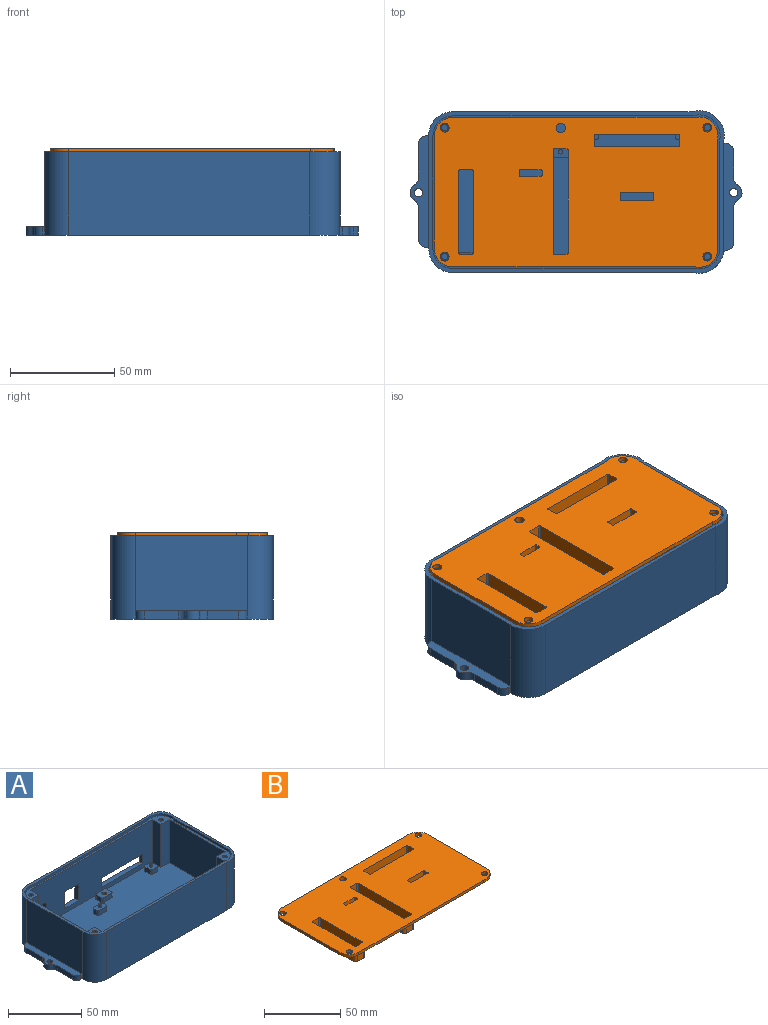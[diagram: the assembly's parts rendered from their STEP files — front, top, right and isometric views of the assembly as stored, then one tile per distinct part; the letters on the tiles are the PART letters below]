
ASSEMBLY  parts=2 mates=1
PART A: 161 faces, bbox 159x77.8x40 mm
  f0: plane 5x4mm, normal (-1,0,0), area 20mm2, adj f1,f7,f8,f9
  f1: cylinder r=1mm len=4mm, axis (0,0,-1), area 6.3mm2, adj f0,f2,f8,f9
  f2: plane 7x4mm, normal (0,-1,0), area 28mm2, adj f1,f3,f8,f9
  f3: cylinder r=1mm len=4mm, axis (0,0,-1), area 6.3mm2, adj f2,f4,f8,f9
  f4: plane 5x4mm, normal (1,0,0), area 20mm2, adj f3,f5,f8,f9
  f5: cylinder r=1mm len=4mm, axis (0,0,-1), area 6.3mm2, adj f4,f6,f8,f9
  f6: plane 7x4mm, normal (0,1,0), area 28mm2, adj f5,f7,f8,f9
  f7: cylinder r=1mm len=4mm, axis (0,0,-1), area 6.3mm2, adj f0,f6,f8,f9
  f8: plane 9x7mm, normal (0,0,1), area 54.1mm2, adj f0,f1,f2,f3,f4,f5,f6,f7
  f9: plane 134x70mm, normal (0,0,1), area 8671mm2, adj f0,f1,f2,f3,f4,f5,f6,f7
  f10: plane 4x3mm, normal (-1,0,0), area 12mm2, adj f9,f11,f17,f18
  f11: cylinder r=1mm len=4mm, axis (0,0,-1), area 6.3mm2, adj f9,f10,f12,f18
  f12: plane 7x4mm, normal (0,-1,0), area 28mm2, adj f9,f11,f13,f18
  f13: cylinder r=1mm len=4mm, axis (0,0,-1), area 6.3mm2, adj f9,f12,f14,f18
  f14: plane 4x3mm, normal (1,0,0), area 12mm2, adj f9,f13,f15,f18
  f15: cylinder r=1mm len=4mm, axis (0,0,-1), area 6.3mm2, adj f9,f14,f16,f18
  f16: plane 7x4mm, normal (0,1,0), area 28mm2, adj f9,f15,f17,f18
  f17: cylinder r=1mm len=4mm, axis (0,0,-1), area 6.3mm2, adj f9,f10,f16,f18
  f18: plane 9x5mm, normal (0,0,1), area 41mm2, adj f10,f11,f12,f13,f14,f15,f16,f17
  f19: plane 118.02x36mm, normal (0,1,0), area 4188.6mm2, adj f9,f27,f28,f32,f81,f86,f87,f89
  f20: plane 118x36mm, normal (0,-1,0), area 3578.4mm2, adj f9,f22,f23,f32,f51,f52,f53,f54
  f21: plane 114.55x40mm, normal (0,1,0), area 3912.4mm2, adj f39,f40,f49,f50,f51,f52,f53,f54
  f22: plane 36x8mm, normal (1,0,0), area 288mm2, adj f9,f20,f31,f32
  f23: plane 36x8mm, normal (-1,0,0), area 288mm2, adj f9,f20,f24,f32
  f24: plane 36x8mm, normal (0,-1,0), area 288mm2, adj f9,f23,f25,f32
  f25: plane 54x36mm, normal (-1,0,0), area 1944mm2, adj f9,f24,f26,f32
  f26: plane 36x8mm, normal (0,1,0), area 288mm2, adj f9,f25,f27,f32
  f27: plane 36x8mm, normal (-1,0,0), area 288mm2, adj f9,f19,f26,f32
  f28: plane 36x8mm, normal (1,0,0), area 288mm2, adj f9,f19,f29,f32
  f29: plane 36x7.98mm, normal (0,1,0), area 287.4mm2, adj f9,f28,f30,f32
  f30: plane 54x36mm, normal (1,0,0), area 1944mm2, adj f9,f29,f31,f32
  f31: plane 36x8mm, normal (0,-1,0), area 288mm2, adj f9,f22,f30,f32
  f32: plane 137.52x73.78mm, normal (0,0,1), area 781.4mm2, adj f19,f20,f22,f23,f24,f25,f26,f27
  f33: plane 53.16x2mm, normal (-1,0,0), area 106.3mm2, adj f32,f37,f38,f49
  f34: plane 114.86x2mm, normal (0,-1,0), area 229.7mm2, adj f32,f38,f46,f49
  f35: plane 53.44x2mm, normal (1,0,0), area 106.9mm2, adj f32,f46,f47,f49
  f36: plane 115.72x2mm, normal (0,1,0), area 231.4mm2, adj f32,f37,f47,f49
  f37: cylinder r=9.77mm len=11.8mm, axis (0,0,-1), area 30.7mm2, adj f32,f33,f36,f49
  f38: cylinder r=10.01mm len=13.15mm, axis (0,0,-1), area 44.2mm2, adj f32,f33,f34,f49
  f39: cylinder r=11.5mm len=40mm, axis (0,0,-1), area 722.6mm2, adj f21,f48,f49,f50,f127
  f40: cylinder r=12.01mm len=40mm, axis (0,0,-1), area 1034.3mm2, adj f21,f41,f49,f50,f140
  f41: plane 51.85x36mm, normal (1,0,0), area 1866.6mm2, adj f40,f42,f49,f144
  f42: extruded ~40x0.3mm, area 13.9mm2, adj f41,f43,f49,f50,f141
  f43: cylinder r=11.77mm len=40mm, axis (0,0,-1), area 777.6mm2, adj f42,f44,f49,f50
  f44: plane 115.49x40mm, normal (0,-1,0), area 4619.6mm2, adj f43,f45,f49,f50
  f45: cylinder r=11.5mm len=40mm, axis (0,0,-1), area 747.2mm2, adj f44,f48,f49,f50,f126
  f46: cylinder r=9.5mm len=9.5mm, axis (0,0,-1), area 29.8mm2, adj f32,f34,f35,f49
  f47: cylinder r=9.5mm len=10.06mm, axis (0,0,-1), area 31mm2, adj f32,f35,f36,f49
  f48: plane 53.38x36mm, normal (-1,0,0), area 1921.9mm2, adj f39,f45,f49,f133
  f49: plane 141.52x77.78mm, normal (0,0,1), area 822.7mm2, adj f21,f33,f34,f35,f36,f37,f38,f39
  f50: plane 159x77.78mm, normal (0,0,-1), area 11301.4mm2, adj f21,f39,f40,f42,f43,f44,f45,f123
  f51: plane 7.85x3.5mm, normal (1,0,0), area 27.5mm2, adj f20,f21,f52,f54
  f52: plane 40x3.5mm, normal (0,0,1), area 140mm2, adj f20,f21,f51,f53
  f53: plane 7.85x3.5mm, normal (-1,0,0), area 27.5mm2, adj f20,f21,f52,f54
  f54: plane 40x3.5mm, normal (0,0,-1), area 140mm2, adj f20,f21,f51,f53
  f55: plane 14x3.5mm, normal (1,0,0), area 49mm2, adj f20,f21,f56,f58
  f56: plane 13.4x3.5mm, normal (0,0,1), area 46.9mm2, adj f20,f21,f55,f57
  f57: plane 14x3.5mm, normal (-1,0,0), area 49mm2, adj f20,f21,f56,f58
  f58: plane 13.4x3.5mm, normal (0,0,-1), area 46.9mm2, adj f20,f21,f55,f57
  f59: plane 12x3.5mm, normal (0,0,-1), area 42mm2, adj f20,f21,f60,f62
  f60: plane 14x3.5mm, normal (1,0,0), area 49mm2, adj f20,f21,f59,f61
  f61: plane 12x3.5mm, normal (0,0,1), area 42mm2, adj f20,f21,f60,f62
  f62: plane 14x3.5mm, normal (-1,0,0), area 49mm2, adj f20,f21,f59,f61
  f63: plane 7x7mm, normal (0,0,1), area 45mm2, adj f64,f65,f66,f67,f68,f69,f70,f71
  f64: cylinder r=1mm len=4mm, axis (0,0,-1), area 6.3mm2, adj f9,f63,f65,f71
  f65: plane 5x4mm, normal (0,1,0), area 20mm2, adj f9,f63,f64,f66
  f66: cylinder r=1mm len=4mm, axis (0,0,-1), area 6.3mm2, adj f9,f63,f65,f67
  f67: plane 5x4mm, normal (1,0,0), area 20mm2, adj f9,f63,f66,f68
  f68: cylinder r=1mm len=4mm, axis (0,0,-1), area 6.3mm2, adj f9,f63,f67,f69
  f69: plane 5x4mm, normal (0,-1,0), area 20mm2, adj f9,f63,f68,f70
  f70: cylinder r=1mm len=4mm, axis (0,0,-1), area 6.3mm2, adj f9,f63,f69,f71
  f71: plane 5x4mm, normal (-1,0,0), area 20mm2, adj f9,f63,f64,f70
  f72: plane 10x7mm, normal (0,0,1), area 61.1mm2, adj f73,f74,f75,f76,f77,f78,f79,f80
  f73: cylinder r=1mm len=4mm, axis (0,0,-1), area 6.3mm2, adj f9,f72,f74,f80
  f74: plane 8x4mm, normal (0,1,0), area 32mm2, adj f9,f72,f73,f75
  f75: cylinder r=1mm len=4mm, axis (0,0,-1), area 6.3mm2, adj f9,f72,f74,f76
  f76: plane 5x4mm, normal (1,0,0), area 20mm2, adj f9,f72,f75,f77
  f77: cylinder r=1mm len=4mm, axis (0,0,-1), area 6.3mm2, adj f9,f72,f76,f78
  f78: plane 8x4mm, normal (0,-1,0), area 32mm2, adj f9,f72,f77,f79
  f79: cylinder r=1mm len=4mm, axis (0,0,-1), area 6.3mm2, adj f9,f72,f78,f80
  f80: plane 5x4mm, normal (-1,0,0), area 20mm2, adj f9,f72,f73,f79
  f81: plane 10x6mm, normal (0,0,1), area 56mm2, adj f19,f82,f83,f84,f85,f86,f87,f88
  f82: cylinder r=1mm len=4mm, axis (0,0,-1), area 6.3mm2, adj f9,f81,f83,f88
  f83: plane 8x4mm, normal (0,1,0), area 32mm2, adj f9,f81,f82,f84
  f84: cylinder r=1mm len=4mm, axis (0,0,-1), area 6.3mm2, adj f9,f81,f83,f85
  f85: plane 4x4mm, normal (1,0,0), area 16mm2, adj f9,f81,f84,f86
  f86: cylinder r=1mm len=4mm, axis (0,0,-1), area 6.3mm2, adj f9,f19,f81,f85
  f87: cylinder r=1mm len=4mm, axis (0,0,-1), area 6.3mm2, adj f9,f19,f81,f88
  f88: plane 4x4mm, normal (-1,0,0), area 16mm2, adj f9,f81,f82,f87
  f89: plane 9x6mm, normal (0,0,1), area 45.1mm2, adj f19,f90,f91,f92,f93,f94,f95,f96
  f90: cylinder r=1mm len=4mm, axis (0,0,-1), area 6.3mm2, adj f9,f19,f89,f96
  f91: cylinder r=1mm len=4mm, axis (0,0,-1), area 6.3mm2, adj f9,f19,f89,f92
  f92: plane 4x4mm, normal (-1,0,0), area 16mm2, adj f9,f89,f91,f93
  f93: cylinder r=1mm len=4mm, axis (0,0,-1), area 6.3mm2, adj f9,f89,f92,f94
  f94: plane 7x4mm, normal (0,1,0), area 28mm2, adj f9,f89,f93,f95
  f95: cylinder r=1mm len=4mm, axis (0,0,-1), area 6.3mm2, adj f9,f89,f94,f96
  f96: plane 4x4mm, normal (1,0,0), area 16mm2, adj f9,f89,f90,f95
  f97: plane 7x7mm, normal (0,0,1), area 45mm2, adj f98,f99,f100,f101,f102,f103,f104,f105
  f98: cylinder r=1mm len=4mm, axis (0,0,-1), area 6.3mm2, adj f9,f97,f99,f105
  f99: plane 5x4mm, normal (0,1,0), area 20mm2, adj f9,f97,f98,f100
  f100: cylinder r=1mm len=4mm, axis (0,0,-1), area 6.3mm2, adj f9,f97,f99,f101
  f101: plane 5x4mm, normal (1,0,0), area 20mm2, adj f9,f97,f100,f102
  f102: cylinder r=1mm len=4mm, axis (0,0,-1), area 6.3mm2, adj f9,f97,f101,f103
  f103: plane 5x4mm, normal (0,-1,0), area 20mm2, adj f9,f97,f102,f104
  f104: cylinder r=1mm len=4mm, axis (0,0,-1), area 6.3mm2, adj f9,f97,f103,f105
  f105: plane 5x4mm, normal (-1,0,0), area 20mm2, adj f9,f97,f98,f104
  f106: plane 10x7mm, normal (0,0,1), area 61.1mm2, adj f107,f108,f109,f110,f111,f112,f113,f114
  f107: cylinder r=1mm len=4mm, axis (0,0,-1), area 6.3mm2, adj f9,f106,f108,f114
  f108: plane 8x4mm, normal (0,1,0), area 32mm2, adj f9,f106,f107,f109
  f109: cylinder r=1mm len=4mm, axis (0,0,-1), area 6.3mm2, adj f9,f106,f108,f110
  f110: plane 5x4mm, normal (1,0,0), area 20mm2, adj f9,f106,f109,f111
  f111: cylinder r=1mm len=4mm, axis (0,0,-1), area 6.3mm2, adj f9,f106,f110,f112
  f112: plane 8x4mm, normal (0,-1,0), area 32mm2, adj f9,f106,f111,f113
  f113: cylinder r=1mm len=4mm, axis (0,0,-1), area 6.3mm2, adj f9,f106,f112,f114
  f114: plane 5x4mm, normal (-1,0,0), area 20mm2, adj f9,f106,f107,f113
  f115: cylinder r=1.6mm len=13mm, axis (0,0,1), area 130.7mm2, adj f32,f116
  f116: plane 3.2x3.2mm, normal (0,0,1), area 8mm2, adj f115
  f117: cylinder r=1.6mm len=13mm, axis (0,0,1), area 130.7mm2, adj f32,f118
  f118: plane 3.2x3.2mm, normal (0,0,1), area 8mm2, adj f117
  f119: cylinder r=1.6mm len=13mm, axis (0,0,1), area 130.7mm2, adj f32,f120
  f120: plane 3.2x3.2mm, normal (0,0,1), area 8mm2, adj f119
  f121: cylinder r=1.6mm len=13mm, axis (0,0,1), area 130.7mm2, adj f32,f122
  f122: plane 3.2x3.2mm, normal (0,0,1), area 8mm2, adj f121
  f123: cylinder r=4mm len=4mm, axis (0,0,-1), area 16.8mm2, adj f50,f124,f132,f133
  f124: plane 15.25x4mm, normal (-1,0,0), area 61mm2, adj f50,f123,f125,f133
  f125: cylinder r=4mm len=4mm, axis (0,0,-1), area 24.7mm2, adj f50,f124,f126,f133
  f126: plane 4x1.1mm, normal (-0.02,-1,0), area 4.4mm2, adj f45,f50,f125,f133
  f127: plane 4x1mm, normal (0,1,0), area 4mm2, adj f39,f50,f128,f133
  f128: cylinder r=4mm len=4mm, axis (0,0,-1), area 25.1mm2, adj f50,f127,f129,f133
  f129: plane 16.25x4mm, normal (-1,0,0), area 65mm2, adj f50,f128,f130,f133
  f130: cylinder r=4mm len=4mm, axis (0,0,-1), area 16.8mm2, adj f50,f129,f132,f133
  f131: cylinder r=2mm len=4mm, axis (0,0,-1), area 50.3mm2, adj f50,f133
  f132: cylinder r=4mm len=6.93mm, axis (0,0,-1), area 33.5mm2, adj f50,f123,f130,f133
  f133: plane 53.38x9mm, normal (0,0,1), area 275.1mm2, adj f48,f123,f124,f125,f126,f127,f128,f129
  f134: plane 16.91x4mm, normal (1,0,0), area 67.7mm2, adj f50,f135,f142,f144
  f135: cylinder r=4mm len=4mm, axis (0,0,-1), area 16.8mm2, adj f50,f134,f136,f144
  f136: cylinder r=4mm len=6.93mm, axis (0,0,-1), area 33.5mm2, adj f50,f135,f137,f144
  f137: cylinder r=4mm len=4mm, axis (0,0,-1), area 16.8mm2, adj f50,f136,f138,f144
  f138: plane 12.68x4mm, normal (1,0,0), area 50.7mm2, adj f50,f137,f139,f144
  f139: cylinder r=4mm len=4mm, axis (0,0,-1), area 23.6mm2, adj f50,f138,f140,f144
  f140: plane 4x1.39mm, normal (0.1,1,0), area 5.6mm2, adj f40,f50,f139,f144
  f141: plane 4x1.78mm, normal (0.2,-0.98,0), area 7.3mm2, adj f42,f50,f142,f144
  f142: cylinder r=4mm len=4mm, axis (0,0,-1), area 22mm2, adj f50,f134,f141,f144
  f143: cylinder r=2mm len=4mm, axis (0,0,-1), area 50.3mm2, adj f50,f144
  f144: plane 51.85x9mm, normal (0,0,1), area 265.8mm2, adj f41,f134,f135,f136,f137,f138,f139,f140
  f145: cylinder r=1.6mm len=4mm, axis (0,0,1), area 40.2mm2, adj f106,f146
  f146: plane 3.2x3.2mm, normal (0,0,1), area 8mm2, adj f145
  f147: cylinder r=1.6mm len=4mm, axis (0,0,1), area 40.2mm2, adj f89,f148
  f148: plane 3.2x3.2mm, normal (0,0,1), area 8mm2, adj f147
  f149: cylinder r=1.6mm len=4mm, axis (0,0,1), area 40.2mm2, adj f72,f150
  f150: plane 3.2x3.2mm, normal (0,0,1), area 8mm2, adj f149
  f151: cylinder r=1.6mm len=4mm, axis (0,0,1), area 40.2mm2, adj f8,f152
  f152: plane 3.2x3.2mm, normal (0,0,1), area 8mm2, adj f151
  f153: cylinder r=1mm len=2.5mm, axis (0,0,-1), area 15.7mm2, adj f81,f154
  f154: plane 2x2mm, normal (0,0,1), area 3.1mm2, adj f153
  f155: cylinder r=1mm len=2.5mm, axis (0,0,-1), area 15.7mm2, adj f18,f156
  f156: plane 2x2mm, normal (0,0,1), area 3.1mm2, adj f155
  f157: cylinder r=1mm len=2.5mm, axis (0,0,-1), area 15.7mm2, adj f63,f158
  f158: plane 2x2mm, normal (0,0,1), area 3.1mm2, adj f157
  f159: cylinder r=1mm len=2.5mm, axis (0,0,-1), area 15.7mm2, adj f97,f160
  f160: plane 2x2mm, normal (0,0,1), area 3.1mm2, adj f159
PART B: 108 faces, bbox 135.8x71.9x11.5 mm
  f0: plane 135.82x71.94mm, normal (0,0,-1), area 8104.9mm2, adj f2,f3,f4,f5,f6,f7,f8,f9
  f1: plane 135.82x71.94mm, normal (0,0,1), area 8589.6mm2, adj f2,f3,f4,f5,f6,f7,f8,f9
  f2: plane 115.72x2mm, normal (0,-1,0), area 231.4mm2, adj f0,f1,f3,f18
  f3: plane 2x0.17mm, normal (-0.12,-0.99,0), area 0.3mm2, adj f0,f1,f2,f4
  f4: cylinder r=8.93mm len=10.9mm, axis (0,0,-1), area 29.3mm2, adj f0,f1,f3,f5
  f5: plane 53.2x2mm, normal (1,0,0), area 106.4mm2, adj f0,f1,f4,f6
  f6: plane 2x0.18mm, normal (0.97,0.24,0), area 0.4mm2, adj f0,f1,f5,f7
  f7: cylinder r=9.01mm len=11.13mm, axis (0,0,-1), area 36.5mm2, adj f0,f1,f6,f8
  f8: plane 115.77x2mm, normal (0,1,0), area 231.5mm2, adj f0,f1,f7,f9
  f9: plane 2x0.3mm, normal (0.02,1,0), area 0.6mm2, adj f0,f1,f8,f10
  f10: cylinder r=8.8mm len=8.8mm, axis (0,0,-1), area 27.6mm2, adj f0,f1,f9,f11
  f11: plane 2x0.02mm, normal (-1,0,0), area 0mm2, adj f0,f1,f10,f12
  f12: plane 48.37x2mm, normal (-1,0,0), area 96.7mm2, adj f0,f1,f11,f13
  f13: plane 5.59x2mm, normal (-1,0,0), area 11.2mm2, adj f0,f1,f12,f14
  f14: cylinder r=8.8mm len=8.82mm, axis (0,0,-1), area 27.7mm2, adj f0,f1,f13,f18
  f15: cylinder r=2.1mm len=4.2mm, axis (0,0,-1), area 26.4mm2, adj f0,f1
  f16: cylinder r=2.1mm len=4.2mm, axis (0,0,-1), area 26.4mm2, adj f0,f1
  f17: cylinder r=2.1mm len=4.2mm, axis (0,0,-1), area 26.4mm2, adj f0,f1
  f18: plane 2x0.03mm, normal (0,-1,0), area 0.1mm2, adj f0,f1,f2,f14
  f19: cylinder r=2.1mm len=4.2mm, axis (0,0,-1), area 26.4mm2, adj f0,f1
  f20: plane 11.5x6mm, normal (0,1,0), area 69mm2, adj f1,f21,f27,f69
  f21: cylinder r=0.5mm len=11.5mm, axis (0,0,-1), area 9mm2, adj f1,f20,f22,f69
  f22: plane 49.5x11.5mm, normal (1,0,0), area 569.2mm2, adj f1,f21,f23,f69
  f23: cylinder r=0.5mm len=11.5mm, axis (0,0,-1), area 9mm2, adj f1,f22,f24,f69
  f24: plane 11.5x6mm, normal (0,-1,0), area 69mm2, adj f1,f23,f25,f69
  f25: cylinder r=0.5mm len=11.5mm, axis (0,0,-1), area 9mm2, adj f1,f24,f26,f69
  f26: plane 49.5x11.5mm, normal (-1,0,0), area 569.2mm2, adj f1,f25,f27,f69
  f27: cylinder r=0.5mm len=11.5mm, axis (0,0,-1), area 9mm2, adj f1,f20,f26,f69
  f28: plane 15x11.5mm, normal (0,1,0), area 172.5mm2, adj f1,f29,f35,f89
  f29: cylinder r=0.5mm len=11.5mm, axis (0,0,-1), area 9mm2, adj f1,f28,f30,f89
  f30: plane 11.5x3mm, normal (1,0,0), area 34.5mm2, adj f1,f29,f31,f89
  f31: cylinder r=0.5mm len=11.5mm, axis (0,0,-1), area 9mm2, adj f1,f30,f32,f89
  f32: plane 15x11.5mm, normal (0,-1,0), area 172.5mm2, adj f1,f31,f33,f89
  f33: cylinder r=0.5mm len=11.5mm, axis (0,0,-1), area 9mm2, adj f1,f32,f34,f89
  f34: plane 11.5x3mm, normal (-1,0,0), area 34.5mm2, adj f1,f33,f35,f89
  f35: cylinder r=0.5mm len=11.5mm, axis (0,0,-1), area 9mm2, adj f1,f28,f34,f89
  f36: plane 38.9x11.5mm, normal (1,0,0), area 447.4mm2, adj f1,f37,f43,f98
  f37: cylinder r=0.8mm len=11.5mm, axis (0,0,-1), area 14.5mm2, adj f1,f36,f38,f98
  f38: plane 11.5x5.4mm, normal (0,-1,0), area 62.1mm2, adj f1,f37,f39,f98
  f39: cylinder r=0.8mm len=11.5mm, axis (0,0,-1), area 14.5mm2, adj f1,f38,f40,f98
  f40: plane 38.9x11.5mm, normal (-1,0,0), area 447.4mm2, adj f1,f39,f41,f98
  f41: cylinder r=0.8mm len=11.5mm, axis (0,0,-1), area 14.5mm2, adj f1,f40,f42,f98
  f42: plane 11.5x5.4mm, normal (0,1,0), area 62.1mm2, adj f1,f41,f43,f98
  f43: cylinder r=0.8mm len=11.5mm, axis (0,0,-1), area 14.5mm2, adj f1,f36,f42,f98
  f44: cylinder r=2.25mm len=11.5mm, axis (0,0,-1), area 162.6mm2, adj f1,f71
  f45: plane 11.5x2mm, normal (1,0,0), area 23mm2, adj f1,f46,f52,f107
  f46: cylinder r=0.5mm len=11.5mm, axis (0,0,-1), area 9mm2, adj f1,f45,f47,f107
  f47: plane 11.5x10mm, normal (0,-1,0), area 115mm2, adj f1,f46,f48,f107
  f48: cylinder r=0.5mm len=11.5mm, axis (0,0,-1), area 9mm2, adj f1,f47,f49,f107
  f49: plane 11.5x2mm, normal (-1,0,0), area 23mm2, adj f1,f48,f50,f107
  f50: cylinder r=0.5mm len=11.5mm, axis (0,0,-1), area 9mm2, adj f1,f49,f51,f107
  f51: plane 11.5x10mm, normal (0,1,0), area 115mm2, adj f1,f50,f52,f107
  f52: cylinder r=0.5mm len=11.5mm, axis (0,0,-1), area 9mm2, adj f1,f45,f51,f107
  f53: plane 40x11.5mm, normal (0,1,0), area 460mm2, adj f1,f54,f60,f80
  f54: cylinder r=0.5mm len=11.5mm, axis (0,0,-1), area 9mm2, adj f1,f53,f55,f80
  f55: plane 11.5x5mm, normal (1,0,0), area 57.5mm2, adj f1,f54,f56,f80
  f56: cylinder r=0.5mm len=11.5mm, axis (0,0,-1), area 9mm2, adj f1,f55,f57,f80
  f57: plane 40x11.5mm, normal (0,-1,0), area 460mm2, adj f1,f56,f58,f80
  f58: cylinder r=0.5mm len=11.5mm, axis (0,0,-1), area 9mm2, adj f1,f57,f59,f80
  f59: plane 11.5x5mm, normal (-1,0,0), area 57.5mm2, adj f1,f58,f60,f80
  f60: cylinder r=0.5mm len=11.5mm, axis (0,0,-1), area 9mm2, adj f1,f53,f59,f80
  f61: plane 49.5x9.5mm, normal (-1,0,0), area 470.2mm2, adj f0,f62,f68,f69
  f62: cylinder r=1.7mm len=9.5mm, axis (0,0,1), area 25.4mm2, adj f0,f61,f63,f69
  f63: plane 9.5x6mm, normal (0,1,0), area 57mm2, adj f0,f62,f64,f69
  f64: cylinder r=1.7mm len=9.5mm, axis (0,0,1), area 25.4mm2, adj f0,f63,f65,f69
  f65: plane 49.5x9.5mm, normal (1,0,0), area 470.2mm2, adj f0,f64,f66,f69
  f66: cylinder r=1.7mm len=9.5mm, axis (0,0,1), area 25.4mm2, adj f0,f65,f67,f69
  f67: plane 9.5x6mm, normal (0,-1,0), area 57mm2, adj f0,f66,f68,f69
  f68: cylinder r=1.7mm len=9.5mm, axis (0,0,1), area 25.4mm2, adj f0,f61,f67,f69
  f69: plane 52.9x9.4mm, normal (0,0,-1), area 141.5mm2, adj f20,f21,f22,f23,f24,f25,f26,f27
  f70: cylinder r=3.45mm len=9.5mm, axis (0,0,1), area 205.9mm2, adj f0,f71
  f71: plane 6.9x6.9mm, normal (0,0,-1), area 21.5mm2, adj f44,f70
  f72: plane 40x9.5mm, normal (0,-1,0), area 380mm2, adj f0,f73,f79,f80
  f73: cylinder r=1.7mm len=9.5mm, axis (0,0,1), area 25.4mm2, adj f0,f72,f74,f80
  f74: plane 9.5x5mm, normal (-1,0,0), area 47.5mm2, adj f0,f73,f75,f80
  f75: cylinder r=1.7mm len=9.5mm, axis (0,0,1), area 25.4mm2, adj f0,f74,f76,f80
  f76: plane 40x9.5mm, normal (0,1,0), area 380mm2, adj f0,f75,f77,f80
  f77: cylinder r=1.7mm len=9.5mm, axis (0,0,1), area 25.4mm2, adj f0,f76,f78,f80
  f78: plane 9.5x5mm, normal (1,0,0), area 47.5mm2, adj f0,f77,f79,f80
  f79: cylinder r=1.7mm len=9.5mm, axis (0,0,1), area 25.4mm2, adj f0,f72,f78,f80
  f80: plane 43.4x8.4mm, normal (0,0,-1), area 116.3mm2, adj f53,f54,f55,f56,f57,f58,f59,f60
  f81: plane 15x9.5mm, normal (0,1,0), area 142.5mm2, adj f0,f82,f88,f89
  f82: cylinder r=1.7mm len=9.5mm, axis (0,0,1), area 25.4mm2, adj f0,f81,f83,f89
  f83: plane 9.5x3mm, normal (1,0,0), area 28.5mm2, adj f0,f82,f84,f89
  f84: cylinder r=1.7mm len=9.5mm, axis (0,0,1), area 25.4mm2, adj f0,f83,f85,f89
  f85: plane 15x9.5mm, normal (0,-1,0), area 142.5mm2, adj f0,f84,f86,f89
  f86: cylinder r=1.7mm len=9.5mm, axis (0,0,1), area 25.4mm2, adj f0,f85,f87,f89
  f87: plane 9.5x3mm, normal (-1,0,0), area 28.5mm2, adj f0,f86,f88,f89
  f88: cylinder r=1.7mm len=9.5mm, axis (0,0,1), area 25.4mm2, adj f0,f81,f87,f89
  f89: plane 18.4x6.4mm, normal (0,0,-1), area 51.5mm2, adj f28,f29,f30,f31,f32,f33,f34,f35
  f90: plane 38.9x9.5mm, normal (-1,0,0), area 369.5mm2, adj f0,f91,f97,f98
  f91: cylinder r=2mm len=9.5mm, axis (0,0,1), area 29.8mm2, adj f0,f90,f92,f98
  f92: plane 9.5x5.4mm, normal (0,1,0), area 51.3mm2, adj f0,f91,f93,f98
  f93: cylinder r=2mm len=9.5mm, axis (0,0,1), area 29.8mm2, adj f0,f92,f94,f98
  f94: plane 38.9x9.5mm, normal (1,0,0), area 369.5mm2, adj f0,f93,f95,f98
  f95: cylinder r=2mm len=9.5mm, axis (0,0,1), area 29.8mm2, adj f0,f94,f96,f98
  f96: plane 9.5x5.4mm, normal (0,-1,0), area 51.3mm2, adj f0,f95,f97,f98
  f97: cylinder r=2mm len=9.5mm, axis (0,0,1), area 29.8mm2, adj f0,f90,f96,f98
  f98: plane 42.9x9.4mm, normal (0,0,-1), area 116.9mm2, adj f36,f37,f38,f39,f40,f41,f42,f43
  f99: plane 9.5x2mm, normal (1,0,0), area 19mm2, adj f0,f100,f106,f107
  f100: cylinder r=1.7mm len=9.5mm, axis (0,0,1), area 25.4mm2, adj f0,f99,f101,f107
  f101: plane 10x9.5mm, normal (0,-1,0), area 95mm2, adj f0,f100,f102,f107
  f102: cylinder r=1.7mm len=9.5mm, axis (0,0,1), area 25.4mm2, adj f0,f101,f103,f107
  f103: plane 9.5x2mm, normal (-1,0,0), area 19mm2, adj f0,f102,f104,f107
  f104: cylinder r=1.7mm len=9.5mm, axis (0,0,1), area 25.4mm2, adj f0,f103,f105,f107
  f105: plane 10x9.5mm, normal (0,1,0), area 95mm2, adj f0,f104,f106,f107
  f106: cylinder r=1.7mm len=9.5mm, axis (0,0,1), area 25.4mm2, adj f0,f99,f105,f107
  f107: plane 13.4x5.4mm, normal (0,0,-1), area 37.1mm2, adj f45,f46,f47,f48,f49,f50,f51,f52
PLACE A t=(2.19,-10.9,8.31)mm
PLACE B t=(41.86,17.55,45.61)mm
MATE cylindrical B.f17 <-> A.f121  axis (0,0,-1) through (-56.87,-9.99,47.61)mm
